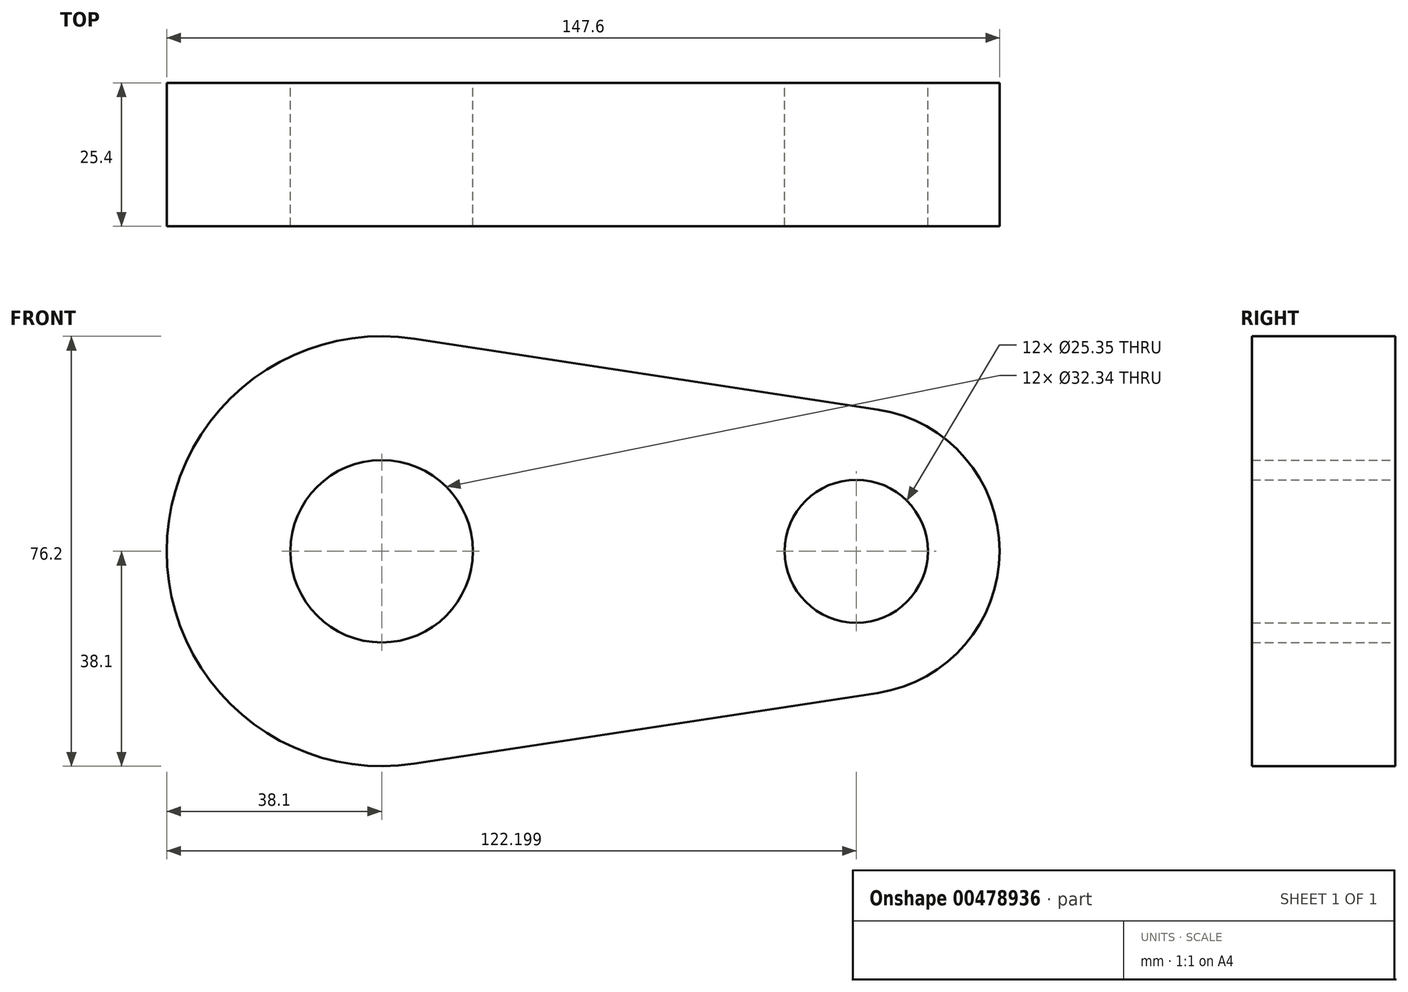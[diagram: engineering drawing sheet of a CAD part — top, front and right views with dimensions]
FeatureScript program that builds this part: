
annotation { "Feature Type Name" : "Feature", "Feature Type Description" : "" }
export const myFeature = defineFeature(function(context is Context, id is Id, definition is map)
    precondition{}
    {
        {
            var Q0;
            Q0=qCreatedBy(makeId("Front.planeOp"),FACE);
            var sketch = newSketch(context, id + "F0", { "sketchPlane" : qUnion([Q0])});
            skCircle(sketch, "E0", {"center": v(0, 0) * mm, "radius": 38.1 * mm});
            skCircle(sketch, "E1", {"center": v(84.1, 0) * mm, "radius": 25.4 * mm});
            skLineSegment(sketch, "E2", {"start": v(5.75, 37.66) * mm, "end": v(87.93, 25.1) * mm});
            skLineSegment(sketch, "E3", {"start": v(5.75, -37.66) * mm, "end": v(87.93, -25.1) * mm});
            skCircle(sketch, "E4", {"center": v(0, 0) * mm, "radius": 16.17 * mm});
            skCircle(sketch, "E5", {"center": v(84.1, 0) * mm, "radius": 12.67 * mm});
            skSolve(sketch);
        }
        {
            var Q0;
            {var subQ0=sQuery(id+"F0.wireOp",EDGE,"E2");Q0=makeQuery(id+"F0.imprint","IMPRINT",FACE,{"disambiguationData":[TD([[makeQuery(id+"F0.imprint","IMPRINT",EDGE,{"derivedFrom":subQ0}),-1.0]])]});}
            var Q1;
            Q1=makeQuery(id+"F0.imprint","IMPRINT",FACE,{"disambiguationData":[TD([[makeQuery(id+"F0.imprint","IMPRINT",EDGE,{"derivedFrom":sQuery(id+"F0.wireOp",EDGE,"E5")}),-1.0]])]});
            var Q2;
            Q2=makeQuery(id+"F0.imprint","IMPRINT",FACE,{"disambiguationData":[TD([[makeQuery(id+"F0.imprint","IMPRINT",EDGE,{"derivedFrom":sQuery(id+"F0.wireOp",EDGE,"E4")}),-1.0]])]});
            extrude(context, id + "F1", {"entities" : qUnion([Q0, Q1, Q2]), "depth" : 25.4 * mm});
        }
    });
